# Revit family: Abutment Slab
name_source: partatom
category: Structural Foundations
revit_build: Autodesk Revit 2016 (Build: 20150714_1515(x64)
units: mm (PartAtom-declared; Revit-internal decimal feet)

## family parameters
Always vertical = Yes
Cap = No
Cut with Voids When Loaded = No
Material for Model Behavior = Concrete
OmniClass Number = 23.25.05.00
OmniClass Title = Foundations
Shared = No
Work Plane-Based = No

## types (1)
- Abutment Slab
    Footing Front Wall Inner Width = 4400 mm
    Footing Front Wall Length = 36700 mm  [stored 120.407 ft]
    Footing Front Wall Outer Width = 2600 mm  [stored 8.53018 ft]
    Footing Height = 1200 mm
    Footing Left Wing Wall Length = 9400 mm
    Footing Left Wing Wall Width = 7000 mm  [stored 22.9659 ft]
    Footing Right Wing Wall Length = 10400 mm  [stored 34.1207 ft]
    Footing Right Wing Wall Width = 8000 mm  [stored 26.2467 ft]
    Length = 0 mm  [stored 0 ft]
    Structural Material = Concrete, C30/37
    Width = 0 mm  [stored 0 ft]

note: [stored X ft] marks values corroborated as IEEE doubles in the binary element streams (Revit-internal decimal feet)

## geometry (parser evidence)
native form markers: Sweep x2
no freeform markers — native parametric forms only
